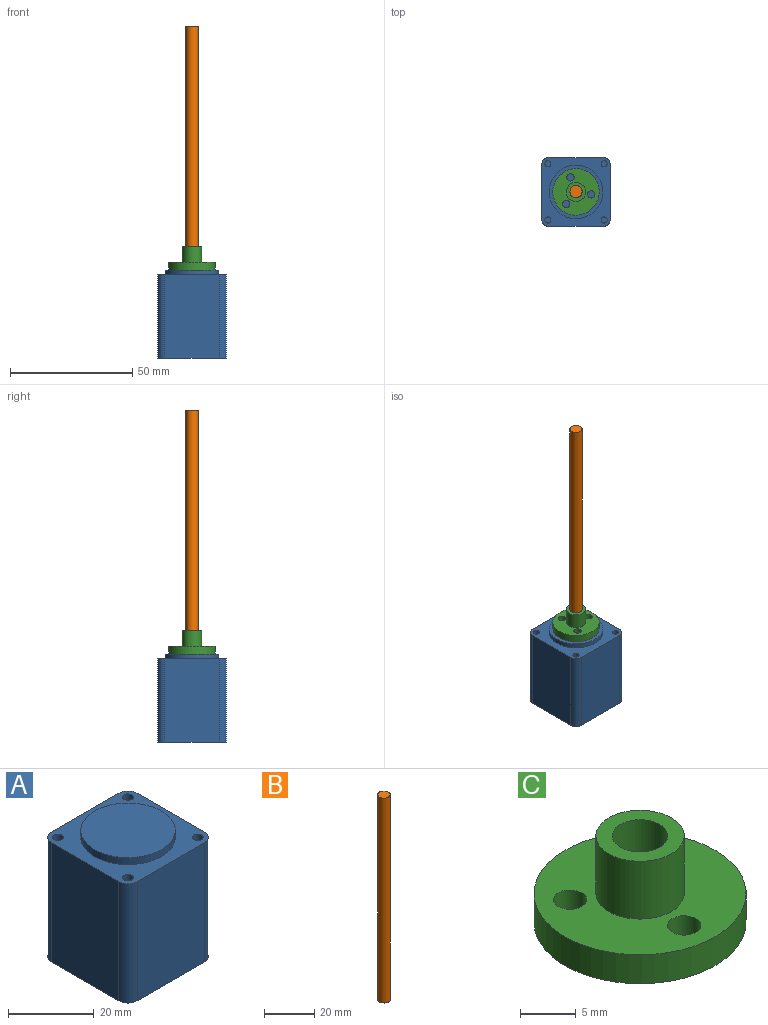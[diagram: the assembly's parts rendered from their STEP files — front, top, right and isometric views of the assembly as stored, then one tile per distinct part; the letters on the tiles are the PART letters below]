
ASSEMBLY  parts=3 mates=2
PART A: 20 faces, bbox 28.2x28.2x36 mm
  f0: plane 28.2x28.2mm, normal (0,0,1), area 387.7mm2, adj f1,f3,f4,f5,f6,f8,f10,f12
  f1: plane 34x22.2mm, normal (-1,0,0), area 754.8mm2, adj f0,f2,f17,f19
  f2: plane 28.2x28.2mm, normal (0,0,-1), area 787.5mm2, adj f1,f3,f4,f5,f16,f17,f18,f19
  f3: plane 34x22.2mm, normal (1,0,0), area 754.8mm2, adj f0,f2,f16,f18
  f4: plane 34x22.2mm, normal (0,-1,0), area 754.8mm2, adj f0,f2,f18,f19
  f5: plane 34x22.2mm, normal (0,1,0), area 754.8mm2, adj f0,f2,f16,f17
  f6: cylinder r=1.25mm len=3.5mm, axis (0,0,1), area 27.5mm2, adj f0,f7
  f7: plane 2.5x2.5mm, normal (0,0,1), area 4.9mm2, adj f6
  f8: cylinder r=1.25mm len=3.5mm, axis (0,0,1), area 27.5mm2, adj f0,f9
  f9: plane 2.5x2.5mm, normal (0,0,1), area 4.9mm2, adj f8
  f10: cylinder r=1.25mm len=3.5mm, axis (0,0,1), area 27.5mm2, adj f0,f11
  f11: plane 2.5x2.5mm, normal (0,0,1), area 4.9mm2, adj f10
  f12: cylinder r=1.25mm len=3.5mm, axis (0,0,1), area 27.5mm2, adj f0,f13
  f13: plane 2.5x2.5mm, normal (0,0,1), area 4.9mm2, adj f12
  f14: cylinder r=11mm len=22mm, axis (0,0,-1), area 138.2mm2, adj f0,f15
  f15: plane 22x22mm, normal (0,0,1), area 380.1mm2, adj f14
  f16: cylinder r=3mm len=34mm, axis (0,0,1), area 160.2mm2, adj f0,f2,f3,f5
  f17: cylinder r=3mm len=34mm, axis (0,0,-1), area 160.2mm2, adj f0,f1,f2,f5
  f18: cylinder r=3mm len=34mm, axis (0,0,-1), area 160.2mm2, adj f0,f2,f3,f4
  f19: cylinder r=3mm len=34mm, axis (0,0,1), area 160.2mm2, adj f0,f1,f2,f4
PART B: 3 faces, bbox 5x5x100 mm
  f0: cylinder r=2.5mm len=100mm, axis (0,0,-1), area 1570.8mm2, adj f1,f2
  f1: plane 5x5mm, normal (0,0,1), area 19.6mm2, adj f0
  f2: plane 5x5mm, normal (0,0,-1), area 19.6mm2, adj f0
PART C: 9 faces, bbox 19.1x19.1x9.5 mm
  f0: cylinder r=2.5mm len=9.53mm, axis (0,0,-1), area 149.7mm2, adj f3,f5
  f1: cylinder r=9.53mm len=19.05mm, axis (0,0,-1), area 190.3mm2, adj f2,f3
  f2: plane 19.05x19.05mm, normal (0,0,1), area 214.3mm2, adj f1,f4,f6,f7,f8
  f3: plane 19.05x19.05mm, normal (0,0,-1), area 244.2mm2, adj f0,f1,f6,f7,f8
  f4: cylinder r=3.97mm len=7.94mm, axis (0,0,-1), area 158.4mm2, adj f2,f5
  f5: plane 7.94x7.94mm, normal (0,0,1), area 29.9mm2, adj f0,f4
  f6: cylinder r=1.5mm len=3.18mm, axis (0,0,-1), area 30mm2, adj f2,f3
  f7: cylinder r=1.5mm len=3.18mm, axis (0,0,-1), area 30mm2, adj f2,f3
  f8: cylinder r=1.5mm len=3.18mm, axis (0,0,-1), area 30mm2, adj f2,f3
PLACE A at identity fixed
PLACE B t=(0,0,2)mm
PLACE C rot(axis=(0,0,1),87.3deg) t=(0,0,0)mm
MATE fastened B.f0 <-> A.f14  axis (0,0,-1) through (0,0,2)mm
MATE cylindrical C.f0 <-> A.f14  axis (0,0,1) through (0,0,2)mm
